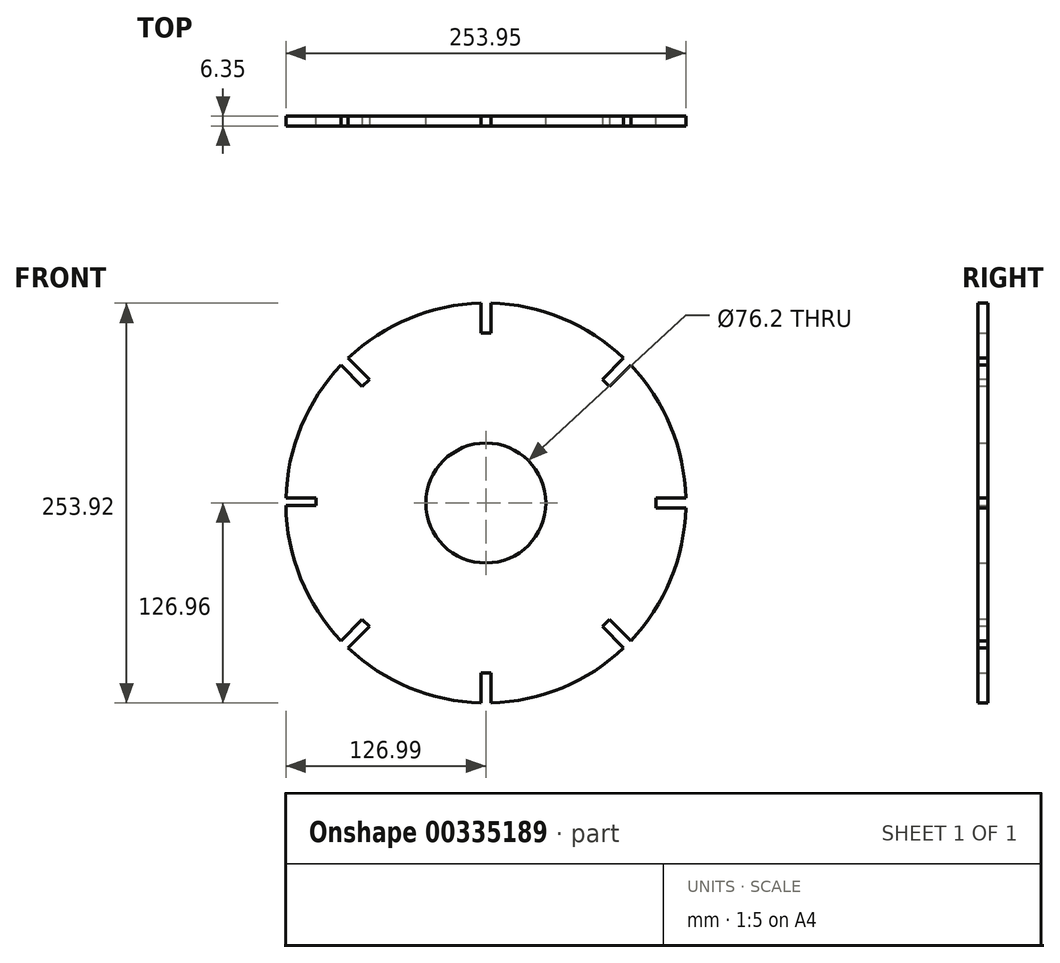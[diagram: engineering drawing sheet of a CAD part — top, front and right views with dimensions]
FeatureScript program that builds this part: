
annotation { "Feature Type Name" : "Feature", "Feature Type Description" : "" }
export const myFeature = defineFeature(function(context is Context, id is Id, definition is map)
    precondition{}
    {
        {
            var Q0;
            Q0=qCreatedBy(makeId("Front.planeOp"),FACE);
            var sketch = newSketch(context, id + "F0", { "sketchPlane" : qUnion([Q0])});
            skCircle(sketch, "E0", {"center": v(0, 0) * mm, "radius": 127 * mm});
            skCircle(sketch, "E1", {"center": v(0, 0) * mm, "radius": 38.1 * mm});
            skLineSegment(sketch, "E2", {"start": v(0, 127) * mm, "end": v(0, -127) * mm, "construction": true});
            skLineSegment(sketch, "E3", {"start": v(127, 0) * mm, "end": v(-127, 0) * mm, "construction": true});
            skLineSegment(sketch, "E4", {"start": v(-3.18, 126.96) * mm, "end": v(-3.17, 107.95) * mm});
            skLineSegment(sketch, "E5", {"start": v(-3.17, 107.95) * mm, "end": v(3.18, 107.95) * mm});
            skLineSegment(sketch, "E6", {"start": v(3.18, 107.95) * mm, "end": v(3.18, 126.96) * mm});
            skLineSegment(sketch, "E7", {"start": v(-126.96, 3.17) * mm, "end": v(-107.91, 3.17) * mm});
            skLineSegment(sketch, "E8", {"start": v(-107.91, 3.17) * mm, "end": v(-107.91, -1.59) * mm});
            skLineSegment(sketch, "E9", {"start": v(-107.91, -1.59) * mm, "end": v(-127, -1.59) * mm});
            skLineSegment(sketch, "E10", {"start": v(-3.17, -126.96) * mm, "end": v(-3.17, -107.91) * mm});
            skLineSegment(sketch, "E11", {"start": v(-3.17, -107.91) * mm, "end": v(3.18, -107.91) * mm});
            skLineSegment(sketch, "E12", {"start": v(3.18, -107.91) * mm, "end": v(3.18, -126.96) * mm});
            skLineSegment(sketch, "E13", {"start": v(126.96, 3.18) * mm, "end": v(107.91, 3.17) * mm});
            skLineSegment(sketch, "E14", {"start": v(107.91, 3.17) * mm, "end": v(107.91, -3.18) * mm});
            skLineSegment(sketch, "E15", {"start": v(107.91, -3.18) * mm, "end": v(126.96, -3.17) * mm});
            skSolve(sketch);
        }
        {
            var Q0;
            Q0=makeQuery(id+"F0.imprint","IMPRINT",FACE,{"disambiguationData":[TD([[makeQuery(id+"F0.imprint","IMPRINT",EDGE,{"derivedFrom":sQuery(id+"F0.wireOp",EDGE,"E1")}),-1.0]])]});
            extrude(context, id + "F1", {"entities" : qUnion([Q0]), "depth" : 6.35 * mm});
        }
        {
            var Q0;
            Q0=makeQuery(id+"F1.opExtrude","CAP_FACE",FACE,{"disambiguationData":[OSD([sQuery(id+"F0.wireOp",EDGE,"E0"),sQuery(id+"F0.wireOp",EDGE,"E1"),sQuery(id+"F0.wireOp",EDGE,"E4"),sQuery(id+"F0.wireOp",EDGE,"E5"),sQuery(id+"F0.wireOp",EDGE,"E6"),sQuery(id+"F0.wireOp",EDGE,"E7"),sQuery(id+"F0.wireOp",EDGE,"E8"),sQuery(id+"F0.wireOp",EDGE,"E9"),sQuery(id+"F0.wireOp",EDGE,"E10"),sQuery(id+"F0.wireOp",EDGE,"E11"),sQuery(id+"F0.wireOp",EDGE,"E12"),sQuery(id+"F0.wireOp",EDGE,"E13"),sQuery(id+"F0.wireOp",EDGE,"E14"),sQuery(id+"F0.wireOp",EDGE,"E15")])],"isStart":false});
            var sketch = newSketch(context, id + "F2", { "sketchPlane" : qUnion([Q0])});
            skLineSegment(sketch, "E16", {"start": v(-89.8, 89.8) * mm, "end": v(89.8, -89.8) * mm});
            skLineSegment(sketch, "E17", {"start": v(89.8, 89.8) * mm, "end": v(-90.36, -90.36) * mm});
            skPoint(sketch, "E17.endSnap0", {"position": v(-90.36, -89.24) * mm});
            skLineSegment(sketch, "E18", {"start": v(-92.02, 87.53) * mm, "end": v(-78.55, 74.06) * mm});
            skLineSegment(sketch, "E19", {"start": v(-78.55, 74.06) * mm, "end": v(-74.06, 78.55) * mm});
            skLineSegment(sketch, "E20", {"start": v(-74.06, 78.55) * mm, "end": v(-87.53, 92.02) * mm});
            skLineSegment(sketch, "E21", {"start": v(-92.02, -87.53) * mm, "end": v(-78.55, -74.06) * mm});
            skLineSegment(sketch, "E22", {"start": v(-78.55, -74.06) * mm, "end": v(-74.06, -78.55) * mm});
            skLineSegment(sketch, "E23", {"start": v(-74.06, -78.55) * mm, "end": v(-87.53, -92.02) * mm});
            skLineSegment(sketch, "E24", {"start": v(74.06, -78.55) * mm, "end": v(78.55, -74.06) * mm});
            skLineSegment(sketch, "E25", {"start": v(78.55, -74.06) * mm, "end": v(92.02, -87.53) * mm});
            skLineSegment(sketch, "E26", {"start": v(74.06, -78.55) * mm, "end": v(87.53, -92.02) * mm});
            skLineSegment(sketch, "E27", {"start": v(87.53, 92.02) * mm, "end": v(74.06, 78.55) * mm});
            skLineSegment(sketch, "E28", {"start": v(74.06, 78.55) * mm, "end": v(78.55, 74.06) * mm});
            skLineSegment(sketch, "E29", {"start": v(78.55, 74.06) * mm, "end": v(92.02, 87.53) * mm});
            skLineSegment(sketch, "E30", {"start": v(-87.53, -92.02) * mm, "end": v(-92.6, -97.24) * mm});
            skLineSegment(sketch, "E31", {"start": v(-92.6, -97.24) * mm, "end": v(-97.25, -92.73) * mm});
            skLineSegment(sketch, "E32", {"start": v(-97.25, -92.73) * mm, "end": v(-92.02, -87.53) * mm});
            skLineSegment(sketch, "E33", {"start": v(-87.53, 92.02) * mm, "end": v(-93.06, 97.55) * mm});
            skLineSegment(sketch, "E34", {"start": v(-93.06, 97.55) * mm, "end": v(-97.7, 92.93) * mm});
            skLineSegment(sketch, "E35", {"start": v(-97.7, 92.93) * mm, "end": v(-92.02, 87.53) * mm});
            skLineSegment(sketch, "E36", {"start": v(87.53, -92.02) * mm, "end": v(97.13, -102.68) * mm});
            skLineSegment(sketch, "E37", {"start": v(97.13, -102.68) * mm, "end": v(102.77, -97.6) * mm});
            skLineSegment(sketch, "E38", {"start": v(102.77, -97.6) * mm, "end": v(92.02, -87.53) * mm});
            skLineSegment(sketch, "E39", {"start": v(87.53, 92.02) * mm, "end": v(92.76, 97.25) * mm});
            skLineSegment(sketch, "E40", {"start": v(92.76, 97.25) * mm, "end": v(97.28, 92.74) * mm});
            skLineSegment(sketch, "E41", {"start": v(97.28, 92.74) * mm, "end": v(92.02, 87.53) * mm});
            skSolve(sketch);
        }
        {
            var Q0;
            Q0 = qSketchRegion(id + "F2", true);
            extrude(context, id + "F3", {"entities" : qUnion([Q0]), "operationType" : NewBodyOperationType.REMOVE, "oppositeDirection" : true, "depth" : 25.4 * mm});
        }
    });
